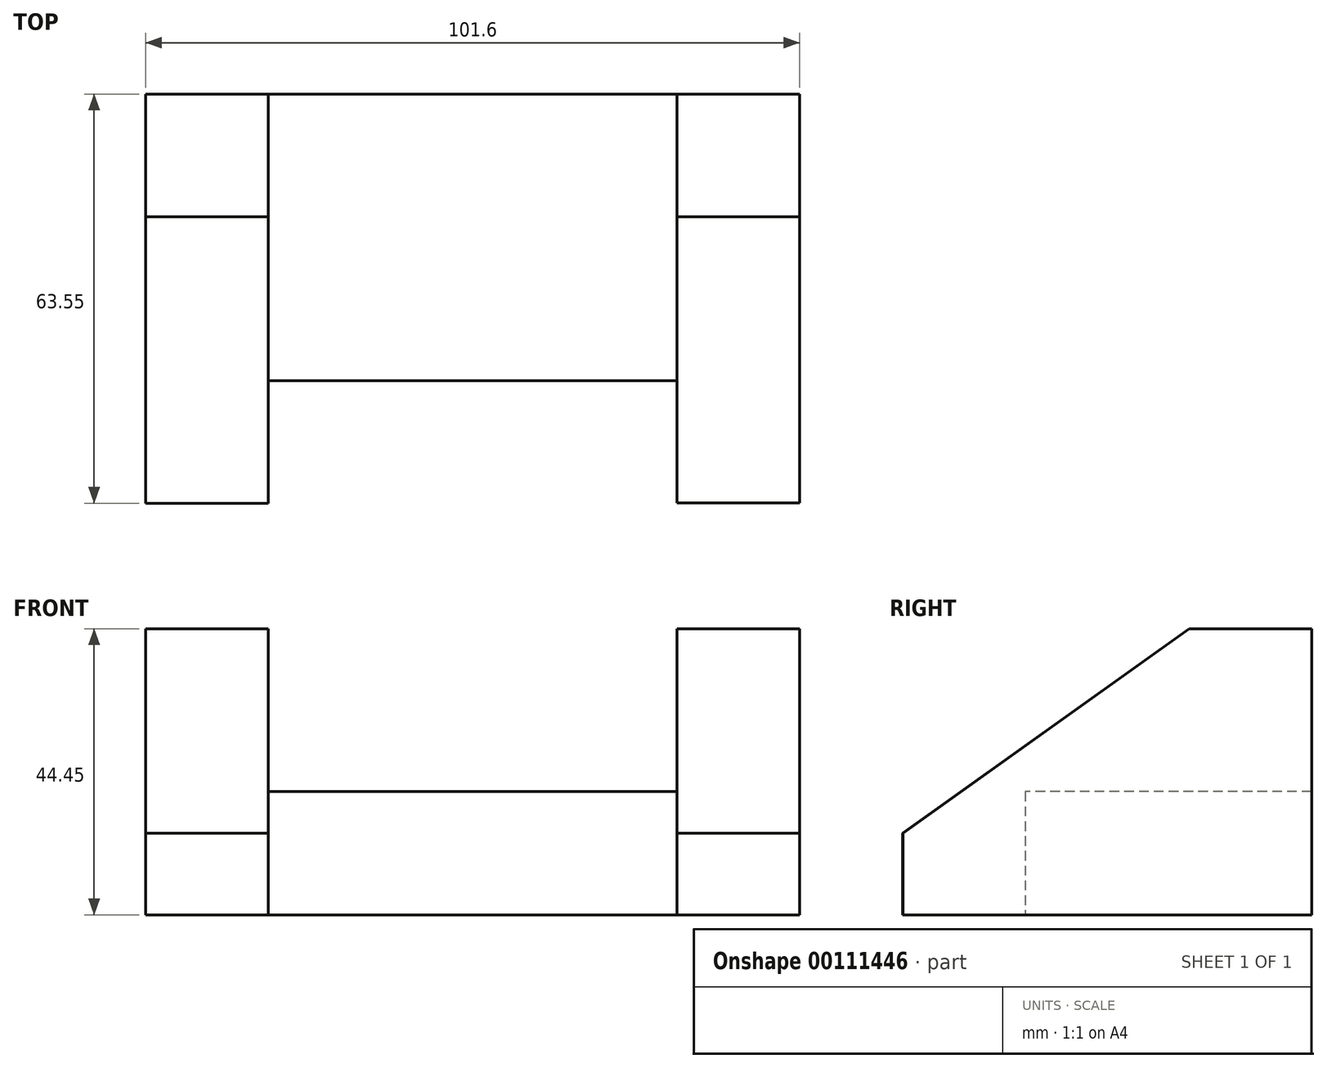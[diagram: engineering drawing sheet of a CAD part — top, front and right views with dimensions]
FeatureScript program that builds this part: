
annotation { "Feature Type Name" : "Feature", "Feature Type Description" : "" }
export const myFeature = defineFeature(function(context is Context, id is Id, definition is map)
    precondition{}
    {
        {
            var Q0;
            Q0=qCreatedBy(makeId("Right.planeOp"),FACE);
            var sketch = newSketch(context, id + "F0", { "sketchPlane" : qUnion([Q0])});
            skLineSegment(sketch, "E0", {"start": v(-30.67, 0) * mm, "end": v(32.88, 0) * mm});
            skLineSegment(sketch, "E1", {"start": v(32.88, 0) * mm, "end": v(32.88, 44.45) * mm});
            skLineSegment(sketch, "E2", {"start": v(32.88, 44.45) * mm, "end": v(13.83, 44.45) * mm});
            skLineSegment(sketch, "E3", {"start": v(-30.67, 0) * mm, "end": v(-30.67, 12.7) * mm});
            skLineSegment(sketch, "E4", {"start": v(-30.67, 12.7) * mm, "end": v(13.83, 44.45) * mm});
            skSolve(sketch);
        }
        {
            var Q0;
            Q0=makeQuery(id+"F0.imprint","IMPRINT",FACE,{"disambiguationData":[TD([[makeQuery(id+"F0.imprint","IMPRINT",EDGE,{"derivedFrom":sQuery(id+"F0.wireOp",EDGE,"E0")}),1.0]])]});
            extrude(context, id + "F1", {"entities" : qUnion([Q0]), "depth" : 19.05 * mm});
        }
        {
            var Q0;
            Q0=makeQuery(id+"F1.opExtrude","CAP_FACE",FACE,{"disambiguationData":[OSD([sQuery(id+"F0.wireOp",EDGE,"E0"),sQuery(id+"F0.wireOp",EDGE,"E1"),sQuery(id+"F0.wireOp",EDGE,"E2"),sQuery(id+"F0.wireOp",EDGE,"E3"),sQuery(id+"F0.wireOp",EDGE,"E4")])],"isStart":false});
            var sketch = newSketch(context, id + "F2", { "sketchPlane" : qUnion([Q0])});
            skLineSegment(sketch, "E5", {"start": v(32.88, 0) * mm, "end": v(32.88, 19.12) * mm});
            skLineSegment(sketch, "E6", {"start": v(32.88, 19.12) * mm, "end": v(-11.62, 19.12) * mm});
            skLineSegment(sketch, "E7", {"start": v(-11.62, 19.12) * mm, "end": v(-11.62, 0) * mm});
            skLineSegment(sketch, "E8", {"start": v(-11.62, 0) * mm, "end": v(-11.62, 19.12) * mm});
            skSolve(sketch);
        }
        {
            var Q0;
            {var subQ0=sQuery(id+"F2.wireOp",EDGE,"E5");Q0=makeQuery(id+"F2.imprint","IMPRINT",FACE,{"disambiguationData":[TD([[makeQuery(id+"F2.imprint","IMPRINT",EDGE,{"derivedFrom":subQ0}),1.0]])]});}
            extrude(context, id + "F3", {"entities" : qUnion([Q0]), "operationType" : NewBodyOperationType.ADD, "depth" : 63.5 * mm});
        }
        {
            var Q0;
            Q0=makeQuery(id+"F3.opExtrude","CAP_FACE",FACE,{"disambiguationData":[OSD([sQuery(id+"F0.wireOp",EDGE,"E0"),sQuery(id+"F2.wireOp",EDGE,"E5"),sQuery(id+"F2.wireOp",EDGE,"E6"),sQuery(id+"F2.wireOp",EDGE,"E8")])],"isStart":false});
            var sketch = newSketch(context, id + "F4", { "sketchPlane" : qUnion([Q0])});
            skLineSegment(sketch, "E9", {"start": v(32.88, 0) * mm, "end": v(32.88, 44.45) * mm});
            skLineSegment(sketch, "E10", {"start": v(32.88, 44.45) * mm, "end": v(13.83, 44.45) * mm});
            skLineSegment(sketch, "E11", {"start": v(13.83, 44.45) * mm, "end": v(-30.62, 12.7) * mm});
            skLineSegment(sketch, "E12", {"start": v(-30.62, 12.7) * mm, "end": v(-30.62, 0) * mm});
            skLineSegment(sketch, "E13", {"start": v(-30.62, 0) * mm, "end": v(32.88, 0) * mm});
            skSolve(sketch);
        }
        {
            var Q0;
            {var subQ1=sQuery(id+"F4.wireOp",EDGE,"E10");Q0=makeQuery(id+"F4.imprint","IMPRINT",FACE,{"disambiguationData":[TD([[makeQuery(id+"F4.imprint","IMPRINT",EDGE,{"derivedFrom":subQ1}),1.0]])]});}
            extrude(context, id + "F5", {"entities" : qUnion([Q0]), "operationType" : NewBodyOperationType.ADD, "depth" : 19.05 * mm});
        }
        {
            var Q0;
            Q0=makeQuery(id+"F3.opExtrude","CAP_FACE",FACE,{"disambiguationData":[OSD([sQuery(id+"F0.wireOp",EDGE,"E0"),sQuery(id+"F2.wireOp",EDGE,"E5"),sQuery(id+"F2.wireOp",EDGE,"E6"),sQuery(id+"F2.wireOp",EDGE,"E8")])],"isStart":false});
            var Q1;
            Q1=makeQuery(id+"F5.opExtrude","CAP_FACE",FACE,{"disambiguationData":[OSD([sQuery(id+"F2.wireOp",EDGE,"E6"),sQuery(id+"F2.wireOp",EDGE,"E8"),sQuery(id+"F4.wireOp",EDGE,"E9"),sQuery(id+"F4.wireOp",EDGE,"E10"),sQuery(id+"F4.wireOp",EDGE,"E11"),sQuery(id+"F4.wireOp",EDGE,"E12"),sQuery(id+"F4.wireOp",EDGE,"E13")])],"isStart":false});
            extrude(context, id + "F6", {"entities" : qUnion([Q0]), "operationType" : NewBodyOperationType.ADD, "endBound" : BoundingType.UP_TO_SURFACE, "endBoundEntityFace" : qUnion([Q1]), "depth" : 25.4 * mm});
        }
    });
